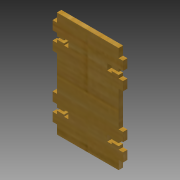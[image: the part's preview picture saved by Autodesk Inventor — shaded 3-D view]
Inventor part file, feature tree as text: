
AUTODESK INVENTOR PART (.ipt)
format: ipt  version: 2014 (Build 180170000, 170)  size: 243,200 bytes
history: native  units: mm
features: sketch x4, plane x3, extrude x3
ambient origin geometry x8: Origin, YZ Plane, XZ Plane, XY Plane, X Axis, Y Axis, Z Axis, Center Point
bodies: Body1 (feature_tree)
feature tree (10):
  sketch  "Sketch1"  dims[d46=10.0mm d47=5.0mm]
  plane  "Work Plane2"
  sketch  "Sketch2"  dims[d48=10.0mm d49=10.0mm]
  plane  "Work Plane3"
  sketch  "Sketch3"  dims[d50=10.0mm d58=10.0mm]
  plane  "Work Plane1"
  sketch  "Sketch4"  dims[d59=5.0mm d60=10.0mm d61=10.0mm d62=10.0mm d70=120.0mm d72=5.0mm d73=0.0mm d75=5.0mm d76=10.0mm d77=10.0mm d78=5.0mm d79=10.0mm d80=40.0mm d81=10.0mm d82=10.0mm d83=10.0mm d84=5.0mm d85=0.0mm d86=5.0mm d87=0.0mm d115=5.0mm d116=7.0mm d117=5.0mm d119=8.0mm d120=2.0mm d121=5.0mm d123=25.0mm d124=1.5mm d125=1.5mm d126=1.5mm d127=1.5mm d128=35.0mm d129=40.0mm d130=70.0mm d131=8.0mm d132=2.0mm]
  extrude  "Extrusion12"  Depth=5.0mm
  extrude  "Extrusion13"  Depth=10.0mm
  extrude  "Extrusion14"  Depth=10.0mm
